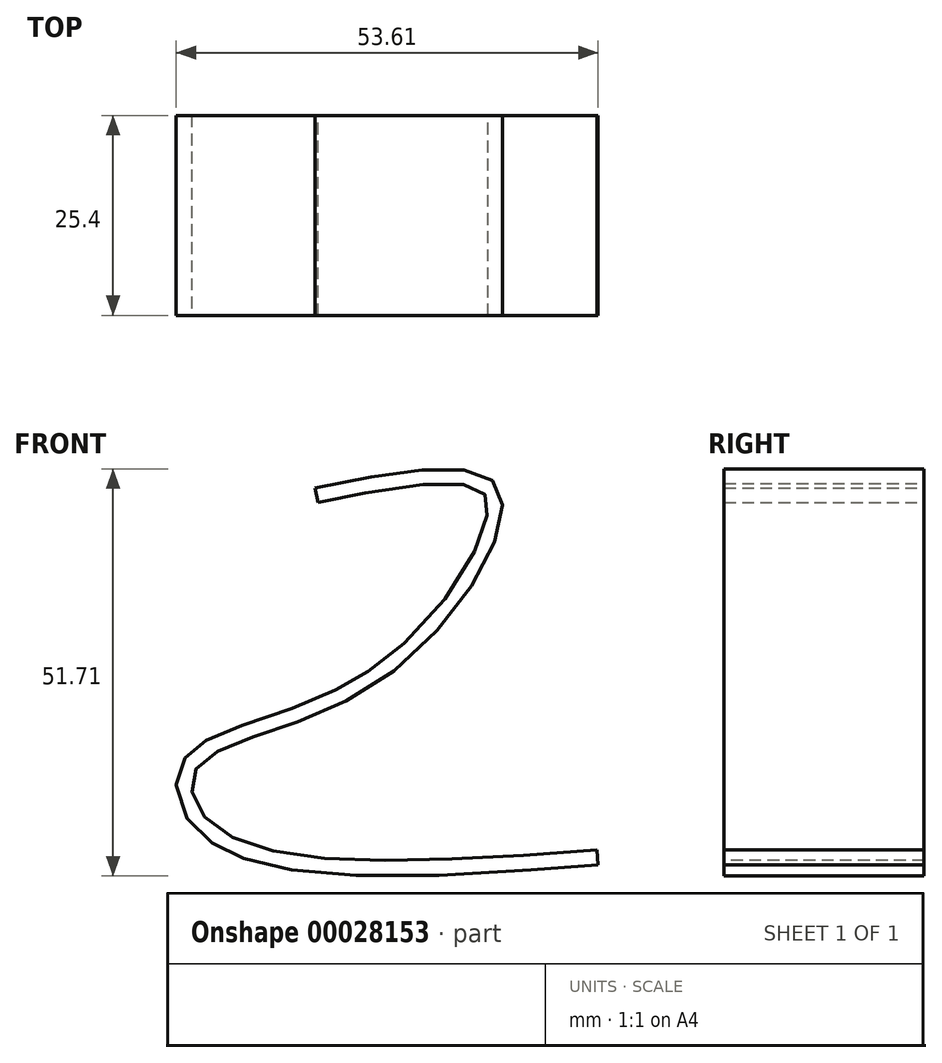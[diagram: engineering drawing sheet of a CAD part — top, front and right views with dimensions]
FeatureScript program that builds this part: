
annotation { "Feature Type Name" : "Feature", "Feature Type Description" : "" }
export const myFeature = defineFeature(function(context is Context, id is Id, definition is map)
    precondition{}
    {
        {
            var Q0;
            Q0=qCreatedBy(makeId("Front.planeOp"),FACE);
            var sketch = newSketch(context, id + "F0", { "sketchPlane" : qUnion([Q0])});
            skFitSpline(sketch, "E0", {"points": [v(27.52, 43.63) * mm, v(50.89, 43.44) * mm, v(35.25, 18.75) * mm, v(12.44, 8.01) * mm, v(15.64, 0) * mm, v(63.33, -2.36) * mm], "startDerivative": vector(165.1, 32.93) * mm, "endDerivative": vector(215.96, 15.89) * mm});
            skFitSpline(sketch, "E1.0", {"points": [v(27.89, 41.79) * mm, v(29.6, 42.13) * mm, v(33.03, 42.81) * mm, v(37.9, 43.66) * mm, v(41.55, 44.09) * mm, v(44.07, 44.18) * mm, v(45.73, 44.11) * mm, v(47.1, 43.9) * mm, v(48.13, 43.57) * mm, v(48.68, 43.24) * mm, v(48.96, 42.98) * mm, v(49.12, 42.77) * mm, v(49.25, 42.53) * mm, v(49.35, 42.22) * mm, v(49.43, 41.81) * mm, v(49.46, 41.15) * mm, v(49.37, 40.12) * mm, v(49, 38.62) * mm, v(48.38, 36.92) * mm, v(47.22, 34.48) * mm, v(45.23, 31.2) * mm, v(42.11, 27.23) * mm, v(39.07, 24.13) * mm, v(36.45, 21.92) * mm, v(34.76, 20.68) * mm, v(33.39, 19.78) * mm, v(31.99, 18.95) * mm, v(30.22, 18) * mm, v(28.06, 17.02) * mm, v(25.2, 15.86) * mm, v(21.7, 14.64) * mm, v(18.46, 13.57) * mm, v(16.13, 12.7) * mm, v(14.52, 12) * mm, v(13.31, 11.32) * mm, v(12.43, 10.7) * mm, v(11.81, 10.18) * mm, v(11.25, 9.6) * mm, v(10.77, 8.92) * mm, v(10.38, 8.2) * mm, v(10.02, 7.17) * mm, v(9.86, 5.84) * mm, v(10.06, 4.26) * mm, v(10.61, 2.75) * mm, v(11.46, 1.32) * mm, v(12.59, 0) * mm, v(13.74, -0.99) * mm, v(14.79, -1.7) * mm, v(15.9, -2.35) * mm, v(17.41, -3.05) * mm, v(19.4, -3.75) * mm, v(22.26, -4.5) * mm, v(26.24, -5.14) * mm, v(31.57, -5.54) * mm, v(39.31, -5.66) * mm, v(49.95, -5.23) * mm, v(58.97, -4.56) * mm, v(63.47, -4.23) * mm]});
            skLineSegment(sketch, "E2", {"start": v(27.52, 43.63) * mm, "end": v(27.89, 41.79) * mm});
            skLineSegment(sketch, "E3", {"start": v(63.33, -2.36) * mm, "end": v(63.47, -4.23) * mm});
            skSolve(sketch);
        }
        {
            var Q0;
            Q0=makeQuery(id+"F0.imprint","IMPRINT",FACE,{"disambiguationData":[TD([[makeQuery(id+"F0.imprint","IMPRINT",EDGE,{"derivedFrom":sQuery(id+"F0.wireOp",EDGE,"E0")}),-1.0]])]});
            extrude(context, id + "F1", {"entities" : qUnion([Q0]), "depth" : 25.4 * mm});
        }
    });
